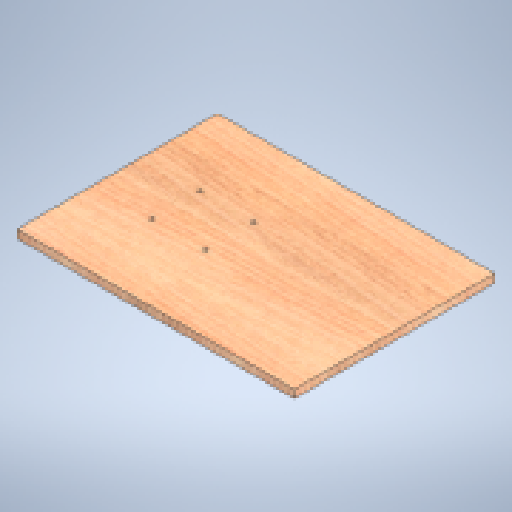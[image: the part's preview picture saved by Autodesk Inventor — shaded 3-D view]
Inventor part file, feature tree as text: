
AUTODESK INVENTOR PART (.ipt)
format: ipt  version: 2024.2 (Build 282272000, 272)  size: 411,648 bytes
history: native  units: mm
features: reference x4, other x4, sketch x3, extrude x2, hole x1
ambient origin geometry x8: Origin, YZ Plane, XZ Plane, XY Plane, X Axis, Y Axis, Z Axis, Center Point
bodies: Body1 (feature_tree)
feature tree (14):
  extrude  "Extrusion4"  Depth=300.0mm
  hole  "Hole3"  [1 undecoded]
  extrude  "Extrusion5"  Depth=10.0mm
  sketch  "Sketch7"  dims[d32=350.0mm d33=300.0mm]
  sketch  "Sketch8"  dims[d34=52.95mm d35=12.0mm d36=0.0mm]
  reference  "Reference2"
  reference  "Reference3"
  reference  "Reference4"
  reference  "Reference5"
  sketch  "Sketch9"  dims[d37=14.0mm d38=5.2mm d39=6.0mm d40=12.0mm d41=3.0mm d42=90.0deg d43=8.0mm d44=20.594885mm d45=65.0mm d46=10.0mm d47=0.0mm]
  other  "0_Entire_Assembly.iam"
  other  "2_Arm:1"
  other  "Aluminum_Profile_4040_100.14mm_bottom:1"
  other  "Aluminum_Profile_4040_100.14mm_top:1"
note: 1 required parameter value undecoded (feature->parameter linkage not recoverable at this tier; creation-order binding heuristic only, values carry confidence <= 0.55)
